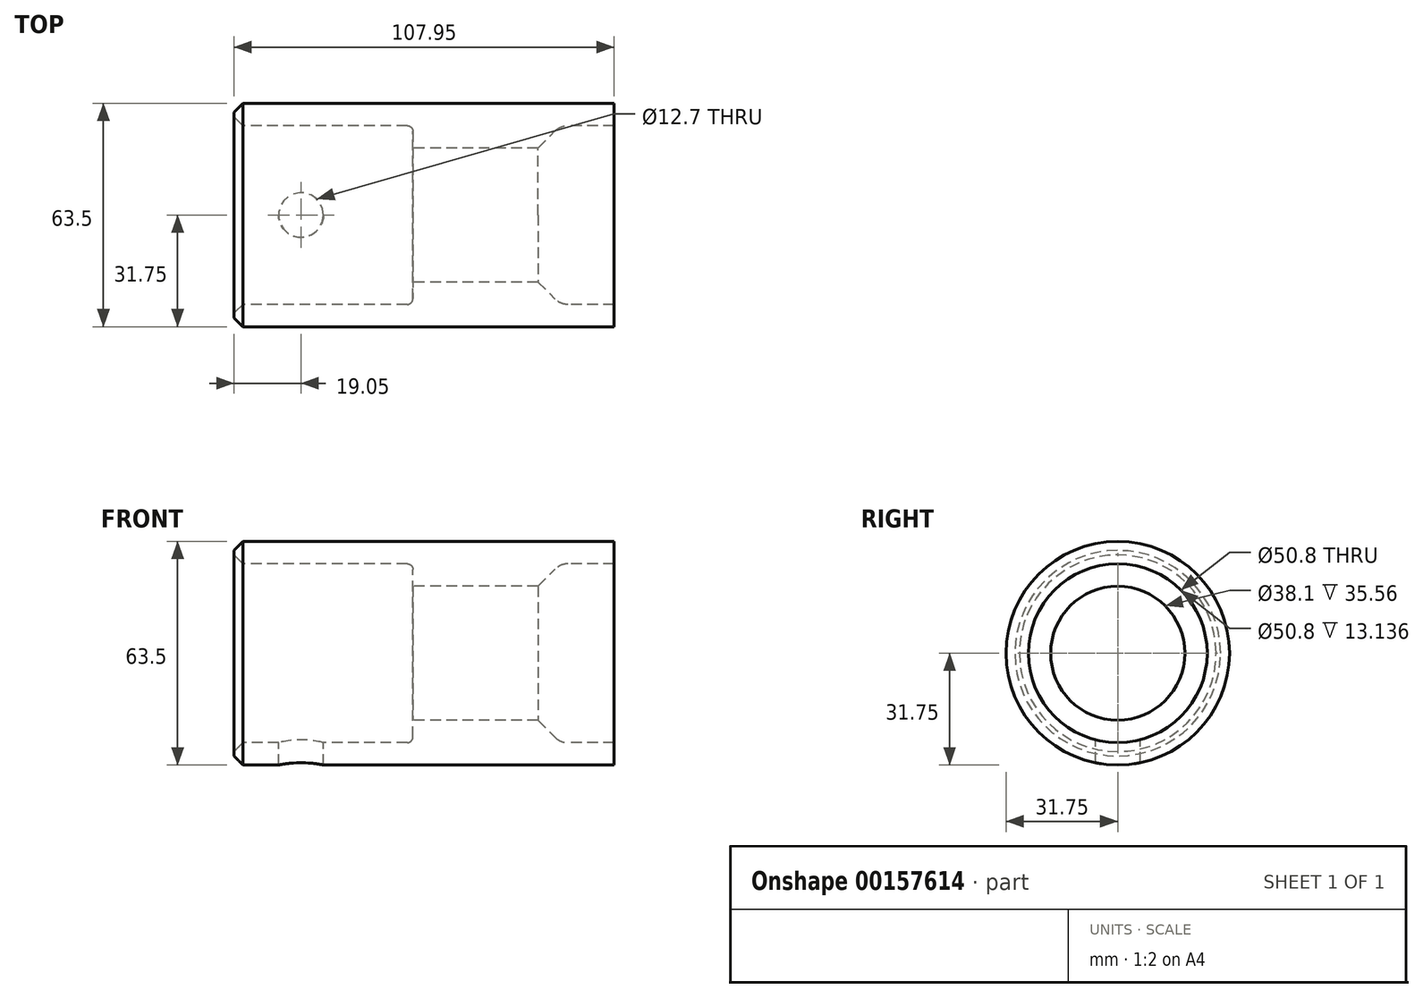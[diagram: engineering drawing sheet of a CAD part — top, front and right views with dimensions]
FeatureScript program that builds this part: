
annotation { "Feature Type Name" : "Feature", "Feature Type Description" : "" }
export const myFeature = defineFeature(function(context is Context, id is Id, definition is map)
    precondition{}
    {
        {
            var Q0;
            Q0=qCreatedBy(makeId("Front.planeOp"),FACE);
            var sketch = newSketch(context, id + "F0", { "sketchPlane" : qUnion([Q0])});
            skLineSegment(sketch, "E0", {"start": v(0, 25.4) * mm, "end": v(50.8, 25.4) * mm});
            skLineSegment(sketch, "E1", {"start": v(50.8, 25.4) * mm, "end": v(50.8, 19.05) * mm});
            skLineSegment(sketch, "E2", {"start": v(50.8, 19.05) * mm, "end": v(86.36, 19.05) * mm});
            skLineSegment(sketch, "E3", {"start": v(86.36, 19.05) * mm, "end": v(92.71, 25.4) * mm});
            skLineSegment(sketch, "E4", {"start": v(92.71, 25.4) * mm, "end": v(107.95, 25.4) * mm});
            skLineSegment(sketch, "E5", {"start": v(107.95, 31.75) * mm, "end": v(0, 31.75) * mm});
            skLineSegment(sketch, "E6", {"start": v(0, 31.75) * mm, "end": v(0, 25.4) * mm});
            skLineSegment(sketch, "E7", {"start": v(107.95, 25.4) * mm, "end": v(107.95, 31.75) * mm});
            skLineSegment(sketch, "E8", {"start": v(0, 0) * mm, "end": v(129.51, 0) * mm, "construction": true});
            skSolve(sketch);
        }
        {
            var Q0;
            Q0=makeQuery(id+"F0.imprint","IMPRINT",FACE,{"disambiguationData":[TD([[makeQuery(id+"F0.imprint","IMPRINT",EDGE,{"derivedFrom":sQuery(id+"F0.wireOp",EDGE,"E0")}),1.0]])]});
            var Q1;
            Q1=sQuery(id+"F0.wireOp",EDGE,"E8");
            revolve(context, id + "F1", {"entities" : qUnion([Q0]), "axis" : qUnion([Q1]), "revolveType" : RevolveType.FULL});
        }
        {
            var Q0;
            Q0=qCreatedBy(makeId("Top.planeOp"),FACE);
            var sketch = newSketch(context, id + "F2", { "sketchPlane" : qUnion([Q0])});
            skCircle(sketch, "E9", {"center": v(19.05, 0) * mm, "radius": 6.35 * mm});
            skSolve(sketch);
        }
        {
            var Q0;
            Q0 = qSketchRegion(id + "F2", true);
            extrude(context, id + "F3", {"entities" : qUnion([Q0]), "operationType" : NewBodyOperationType.REMOVE, "endBound" : BoundingType.THROUGH_ALL, "oppositeDirection" : true, "depth" : 25.4 * mm});
        }
        {
            var Q0;
            Q0=makeQuery(id+"F1.opRevolve","SWEPT_EDGE",EDGE,{"disambiguationData":[OSD([sQuery(id+"F0.wireOp",EDGE,"E0"),sQuery(id+"F0.wireOp",EDGE,"E1")])]});
            fillet(context, id + "F4", {"entities" : qUnion([Q0]), "radius" : 1.59 * mm, "tangentPropagation" : true, "allowEdgeOverflow" : false});
        }
        {
            var Q0;
            Q0=makeQuery(id+"F1.opRevolve","SWEPT_EDGE",EDGE,{"disambiguationData":[OSD([sQuery(id+"F0.wireOp",EDGE,"E0"),sQuery(id+"F0.wireOp",EDGE,"E6")])]});
            var Q1;
            Q1=makeQuery(id+"F1.opRevolve","SWEPT_EDGE",EDGE,{"disambiguationData":[OSD([sQuery(id+"F0.wireOp",EDGE,"E5"),sQuery(id+"F0.wireOp",EDGE,"E6")])]});
            chamfer(context, id + "F5", {"entities" : qUnion([Q0, Q1]), "width" : 2.54 * mm, "tangentPropagation" : true});
        }
        {
            var Q0;
            Q0=makeQuery(id+"F1.opRevolve","SWEPT_EDGE",EDGE,{"disambiguationData":[OSD([sQuery(id+"F0.wireOp",EDGE,"E3"),sQuery(id+"F0.wireOp",EDGE,"E4")])]});
            fillet(context, id + "F6", {"entities" : qUnion([Q0]), "radius" : 5.08 * mm, "tangentPropagation" : true, "allowEdgeOverflow" : false});
        }
    });
